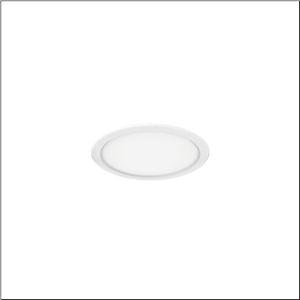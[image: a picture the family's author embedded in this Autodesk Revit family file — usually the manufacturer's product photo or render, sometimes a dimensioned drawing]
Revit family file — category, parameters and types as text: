
# Revit family: lunis_41_eco_51ds107d43a
name_source: partatom
category: Lighting Fixtures
units: mm (PartAtom-declared; Revit-internal decimal feet)

## family parameters
Cut with Voids When Loaded = No
Host = Face
Light Source = No
Part Type = Normal
Room Calculation Point = No
Round Connector Dimension = Use Diameter
Shared = No

## types (1)
- Lunis 41 ECO (1 x LED, 1460 lm, 14 W, 4000K)
    Apparent Load = 14 VA
    CIE Flux Codes = 47 80 97 100 100
    Color Rendering = 80
    Color Temperature = 4000K
    Default Elevation = 1800 mm
    Description = Lunis 41,  ECO, downlight, light emission: direct distribution, LED rated luminous flux: 1.460lm, light colour: 840, control gear: ECG, mains connection: 230V, AC, 50/60Hz, housing, round, of aluminium, coated, traffic white (RAL 9016), diameter: 166mm, recess depth: 54mm, protection rating (complete): IP20, protection rating (on room side): IP40, insulation class (complete): insulation class II (safety insulation), certification: CE, permissible ambient temperature for indoor applications: -20..+40°C, packaging unit: 1 piece
    Height = 0 mm  [stored 0 ft]
    Lamp = 1 x LED
    Lamp Light Flux = 1460 lm
    Lamp Power = 14 W
    Lamp count = 1
    Length = 165 mm
    Luminous efficacy = 104 lm/W
    Manufacturer = Siteco
    ModVariant = No
    Model = 51DS107D43A
    Mounting Place = Ceiling
    Mounting Type = Recessed
    Number of Poles = 1
    OnlyDefault = Yes
    Power Factor = 1
    Product Name = Lunis 41 ECO
    Product group = downlight
    ProductGroupID = 400
    Protection Class = Protection class II
    Protection Degree = IP 20
    RLX_Detail_Level = 1
    RLX_Emergency_Light_Flux = 0 lm
    RLX_Emergency_Type = 0
    RLX_Emergency_Type_DB = No
    RlxData = <blob elided: 25709 chars, md5=c426f38c>
    Socket = socket
    Standby Power = 0 W
    System Light Flux = 1460 lm
    System Power = 14 W
    Type Comments = Product without accessories
    Type Image = l_1007041.jpg
    URL = http://relux.com
    VarID = ---
    Voltage = 0 V
    Weight = 0.00 kg
    Width = 0 mm  [stored 0 ft]

note: [stored X ft] marks values corroborated as IEEE doubles in the binary element streams (Revit-internal decimal feet)

## geometry (parser evidence)
native form markers: Blend x4, Sweep x9
no freeform markers — native parametric forms only
